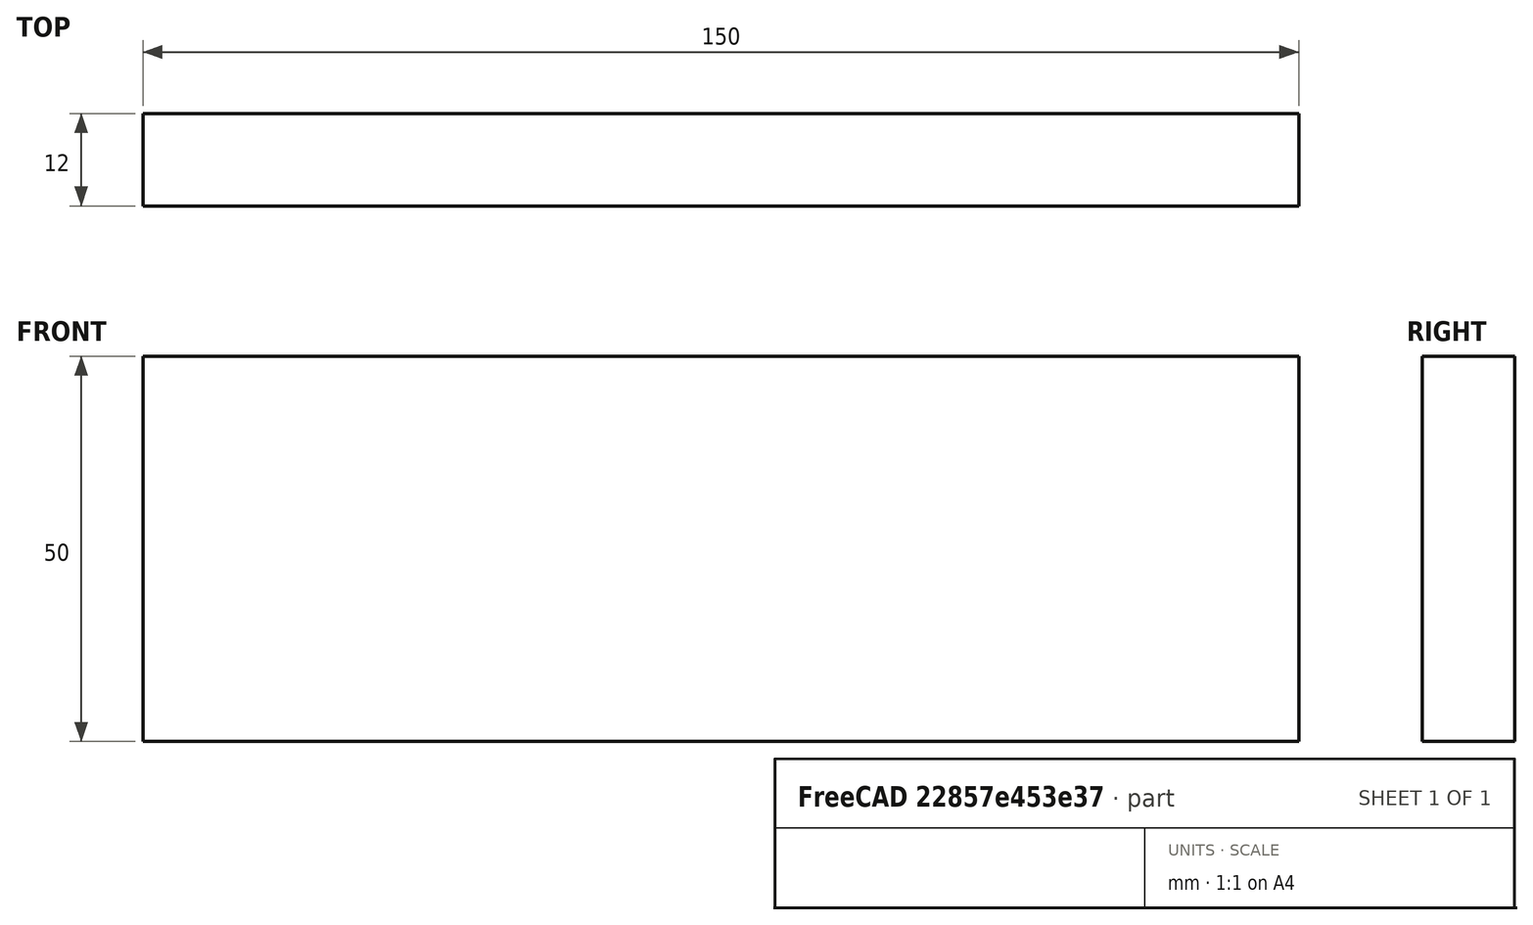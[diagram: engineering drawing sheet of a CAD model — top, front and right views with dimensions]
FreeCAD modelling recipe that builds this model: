
FCSTD DOCUMENT  (FreeCAD 0.15R4671 (Git))
Label: Flat Bar 150x12 EN10058 S235JR
License: All rights reserved
LicenseURL: http://en.wikipedia.org/wiki/All_rights_reserved
objects: Sketcher::SketchObject×1, Part::Extrusion×1
note: 2 computed .brp shape members not serialized (recipe doc carries the construction recipe); baked Part::Feature solids carry a one-line shape summary decoded from their .brp

FEATURE [Sketcher::SketchObject] Sketch
  sketch-geometry (4):
    g0: LineSegment StartX=-75 StartY=-6 StartZ=0 EndX=75 EndY=-6 EndZ=0
    g1: LineSegment StartX=75 StartY=-6 StartZ=0 EndX=75 EndY=6 EndZ=0
    g2: LineSegment StartX=75 StartY=6 StartZ=0 EndX=-75 EndY=6 EndZ=0
    g3: LineSegment StartX=-75 StartY=6 StartZ=0 EndX=-75 EndY=-6 EndZ=0
  constraints (12):
    c: Coincident(g0,g1)
    c: Coincident(g1,g2)
    c: Coincident(g2,g3)
    c: Coincident(g3,g0)
    c: Horizontal(g0)
    c: Horizontal(g2)
    c: Vertical(g1)
    c: Vertical(g3)
    c: Symmetric(g1,g2,g-2)
    c: Symmetric(g0,g1,g-1)
    c: DistanceY(g1) = 12
    c: DistanceX(g0) = 150
FEATURE [Part::Extrusion] Extrude  label="Flat Bar 150x12 EN10058 S235JR"
  Base = -> Sketch
  Dir = (0,0,50)
  Solid = true
